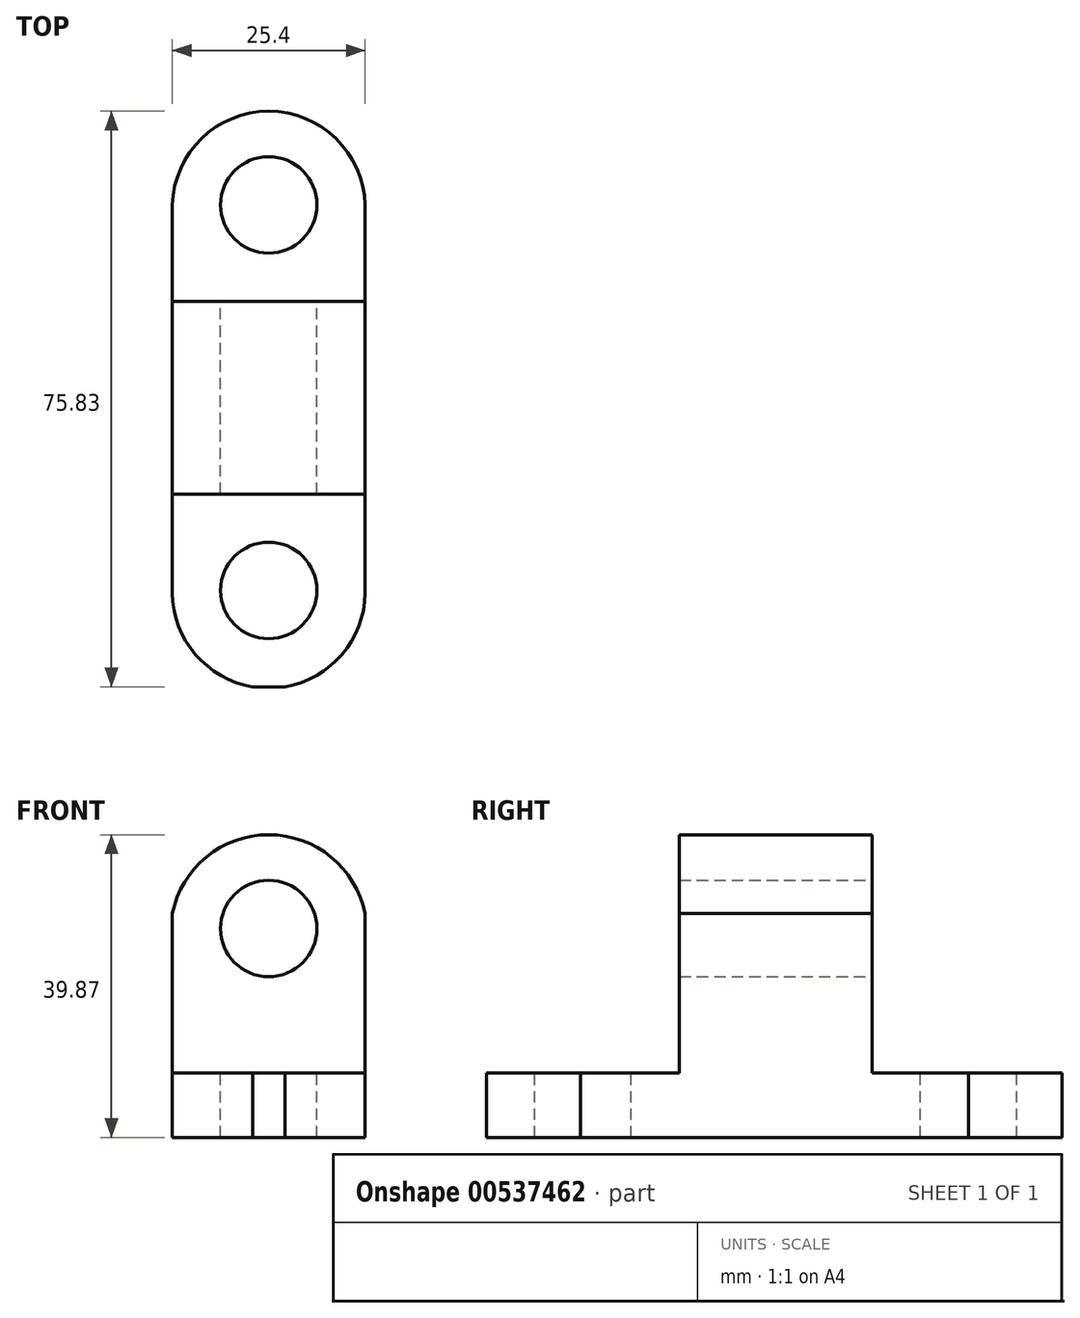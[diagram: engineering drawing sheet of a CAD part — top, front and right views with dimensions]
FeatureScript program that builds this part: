
annotation { "Feature Type Name" : "Feature", "Feature Type Description" : "" }
export const myFeature = defineFeature(function(context is Context, id is Id, definition is map)
    precondition{}
    {
        {
            var Q0;
            Q0=qCreatedBy(makeId("Right.planeOp"),FACE);
            var sketch = newSketch(context, id + "F0", { "sketchPlane" : qUnion([Q0])});
            skLineSegment(sketch, "E0", {"start": v(0, 0) * mm, "end": v(76.2, 0) * mm});
            skLineSegment(sketch, "E1", {"start": v(76.2, 0) * mm, "end": v(76.2, 8.47) * mm});
            skLineSegment(sketch, "E2", {"start": v(76.2, 8.47) * mm, "end": v(50.8, 8.47) * mm});
            skLineSegment(sketch, "E3", {"start": v(50.8, 8.47) * mm, "end": v(50.8, 40.22) * mm});
            skLineSegment(sketch, "E4", {"start": v(50.8, 40.22) * mm, "end": v(25.4, 40.22) * mm});
            skLineSegment(sketch, "E5", {"start": v(25.4, 40.22) * mm, "end": v(25.4, 8.47) * mm});
            skLineSegment(sketch, "E6", {"start": v(25.4, 8.47) * mm, "end": v(0, 8.47) * mm});
            skLineSegment(sketch, "E7", {"start": v(0, 8.47) * mm, "end": v(0, 0) * mm});
            skSolve(sketch);
        }
        {
            var Q0;
            Q0=makeQuery(id+"F0.imprint","IMPRINT",FACE,{"disambiguationData":[TD([[makeQuery(id+"F0.imprint","IMPRINT",EDGE,{"derivedFrom":sQuery(id+"F0.wireOp",EDGE,"E0")}),1.0]])]});
            extrude(context, id + "F1", {"entities" : qUnion([Q0]), "depth" : 25.4 * mm, "offsetDistance" : 25.4 * mm});
        }
        {
            var Q0;
            Q0=makeQuery(id+"F1.opExtrude","SWEPT_FACE",FACE,{"disambiguationData":[OSD([sQuery(id+"F0.wireOp",EDGE,"E3")])]});
            var sketch = newSketch(context, id + "F2", { "sketchPlane" : qUnion([Q0])});
            skCircle(sketch, "E8", {"center": v(-12.7, 27.52) * mm, "radius": 6.35 * mm});
            skSolve(sketch);
        }
        {
            var Q0;
            Q0=makeQuery(id+"F2.imprint","IMPRINT",FACE,{"disambiguationData":[TD([[makeQuery(id+"F2.imprint","IMPRINT",EDGE,{"derivedFrom":sQuery(id+"F2.wireOp",EDGE,"E8")}),1.0]])]});
            extrude(context, id + "F3", {"entities" : qUnion([Q0]), "operationType" : NewBodyOperationType.REMOVE, "oppositeDirection" : true, "depth" : 25.4 * mm, "offsetDistance" : 25.4 * mm});
        }
        {
            var Q0;
            Q0=makeQuery(id+"F1.opExtrude","SWEPT_FACE",FACE,{"disambiguationData":[OSD([sQuery(id+"F0.wireOp",EDGE,"E2")])]});
            var sketch = newSketch(context, id + "F4", { "sketchPlane" : qUnion([Q0])});
            skCircle(sketch, "E9", {"center": v(12.7, 63.5) * mm, "radius": 6.35 * mm});
            skCircle(sketch, "E10", {"center": v(12.7, 12.7) * mm, "radius": 6.35 * mm});
            skSolve(sketch);
        }
        {
            var Q0;
            Q0=makeQuery(id+"F4.imprint","IMPRINT",FACE,{"disambiguationData":[TD([[makeQuery(id+"F4.imprint","IMPRINT",EDGE,{"derivedFrom":sQuery(id+"F4.wireOp",EDGE,"E9")}),1.0]])]});
            var Q1;
            Q1=makeQuery(id+"F4.imprint","IMPRINT",FACE,{"disambiguationData":[TD([[makeQuery(id+"F4.imprint","IMPRINT",EDGE,{"derivedFrom":sQuery(id+"F4.wireOp",EDGE,"E10")}),1.0]])]});
            extrude(context, id + "F5", {"entities" : qUnion([Q0, Q1]), "operationType" : NewBodyOperationType.REMOVE, "oppositeDirection" : true, "depth" : 25.4 * mm, "offsetDistance" : 25.4 * mm});
        }
        {
            var Q0;
            Q0=makeQuery(id+"F1.opExtrude","SWEPT_FACE",FACE,{"disambiguationData":[OSD([sQuery(id+"F0.wireOp",EDGE,"E2")])]});
            var sketch = newSketch(context, id + "F6", { "sketchPlane" : qUnion([Q0])});
            skArc(sketch, "E11", {"start": v(25.4, 63.5) * mm, "mid": v(12.7, 75.83) * mm, "end": v(0, 63.5) * mm});
            skArc(sketch, "E12", {"start": v(0, 12.56) * mm, "mid": v(13.35, -0.15) * mm, "end": v(25.4, 13.8) * mm});
            skSolve(sketch);
        }
        {
            var Q0;
            {var subQ0=sQuery(id+"F6.wireOp",EDGE,"E11");Q0=makeQuery(id+"F6.imprint","IMPRINT",FACE,{"disambiguationData":[TD([[makeQuery(id+"F6.imprint","IMPRINT",EDGE,{"derivedFrom":subQ0}),-1.0]])]});}
            extrude(context, id + "F7", {"entities" : qUnion([Q0]), "operationType" : NewBodyOperationType.REMOVE, "oppositeDirection" : true, "depth" : 25.4 * mm, "offsetDistance" : 25.4 * mm});
        }
        {
            var Q0;
            Q0=makeQuery(id+"F1.opExtrude","SWEPT_FACE",FACE,{"disambiguationData":[OSD([sQuery(id+"F0.wireOp",EDGE,"E6")])]});
            var sketch = newSketch(context, id + "F8", { "sketchPlane" : qUnion([Q0])});
            skArc(sketch, "E13", {"start": v(0, 12.7) * mm, "mid": v(12.7, -0.18) * mm, "end": v(25.4, 12.7) * mm});
            skSolve(sketch);
        }
        {
            var Q0;
            {var subQ0=sQuery(id+"F8.wireOp",EDGE,"E13");var subQ1=sQuery(id+"F0.wireOp",EDGE,"E6");var subQ2=makeQuery(id+"F1.opExtrude","CAP_EDGE",EDGE,{"disambiguationData":[OSD([subQ1])],"isStart":true});var subQ3=makeQuery(id+"F8.imprint","INTERSECT",VERTEX,{"disambiguationData":[OD(1.0)],"derivedFrom":[subQ2,subQ0]});Q0=makeQuery(id+"F8.imprint","IMPRINT",FACE,{"disambiguationData":[TD([[makeQuery(id+"F8.imprint","IMPRINT",EDGE,{"disambiguationData":[TD([[subQ3,-1.0]])],"derivedFrom":subQ0}),-1.0]])]});}
            var Q1;
            {var subQ0=sQuery(id+"F8.wireOp",EDGE,"E13");var subQ1=sQuery(id+"F0.wireOp",EDGE,"E6");var subQ4=makeQuery(id+"F1.opExtrude","CAP_EDGE",EDGE,{"disambiguationData":[OSD([subQ1])],"isStart":false});var subQ5=makeQuery(id+"F8.imprint","INTERSECT",VERTEX,{"disambiguationData":[OD(1.0)],"derivedFrom":[subQ4,subQ0]});Q1=makeQuery(id+"F8.imprint","IMPRINT",FACE,{"disambiguationData":[TD([[makeQuery(id+"F8.imprint","IMPRINT",EDGE,{"disambiguationData":[TD([[subQ5,1.0]])],"derivedFrom":subQ0}),-1.0]])]});}
            extrude(context, id + "F9", {"entities" : qUnion([Q0, Q1]), "operationType" : NewBodyOperationType.REMOVE, "oppositeDirection" : true, "depth" : 25.4 * mm, "offsetDistance" : 25.4 * mm});
        }
        {
            var Q0;
            Q0=makeQuery(id+"F1.opExtrude","SWEPT_FACE",FACE,{"disambiguationData":[OSD([sQuery(id+"F0.wireOp",EDGE,"E5")])]});
            var sketch = newSketch(context, id + "F10", { "sketchPlane" : qUnion([Q0])});
            skArc(sketch, "E14", {"start": v(25.4, 24.34) * mm, "mid": v(12.7, 39.87) * mm, "end": v(0, 24.34) * mm});
            skSolve(sketch);
        }
        {
            var Q0;
            Q0 = qSketchRegion(id + "F10", true);
            var Q1;
            {var subQ1=sQuery(id+"F0.wireOp",EDGE,"E5");var subQ6=makeQuery(id+"F1.opExtrude","SWEPT_EDGE",EDGE,{"disambiguationData":[OSD([sQuery(id+"F0.wireOp",EDGE,"E4"),subQ1])]});Q1=makeQuery(id+"F10.imprint","IMPRINT",FACE,{"disambiguationData":[TD([[makeQuery(id+"F10.imprint","IMPRINT",EDGE,{"derivedFrom":subQ6}),1.0]])]});}
            extrude(context, id + "F11", {"entities" : qUnion([Q0, Q1]), "operationType" : NewBodyOperationType.REMOVE, "oppositeDirection" : true, "depth" : 25.4 * mm, "offsetDistance" : 25.4 * mm});
        }
    });
